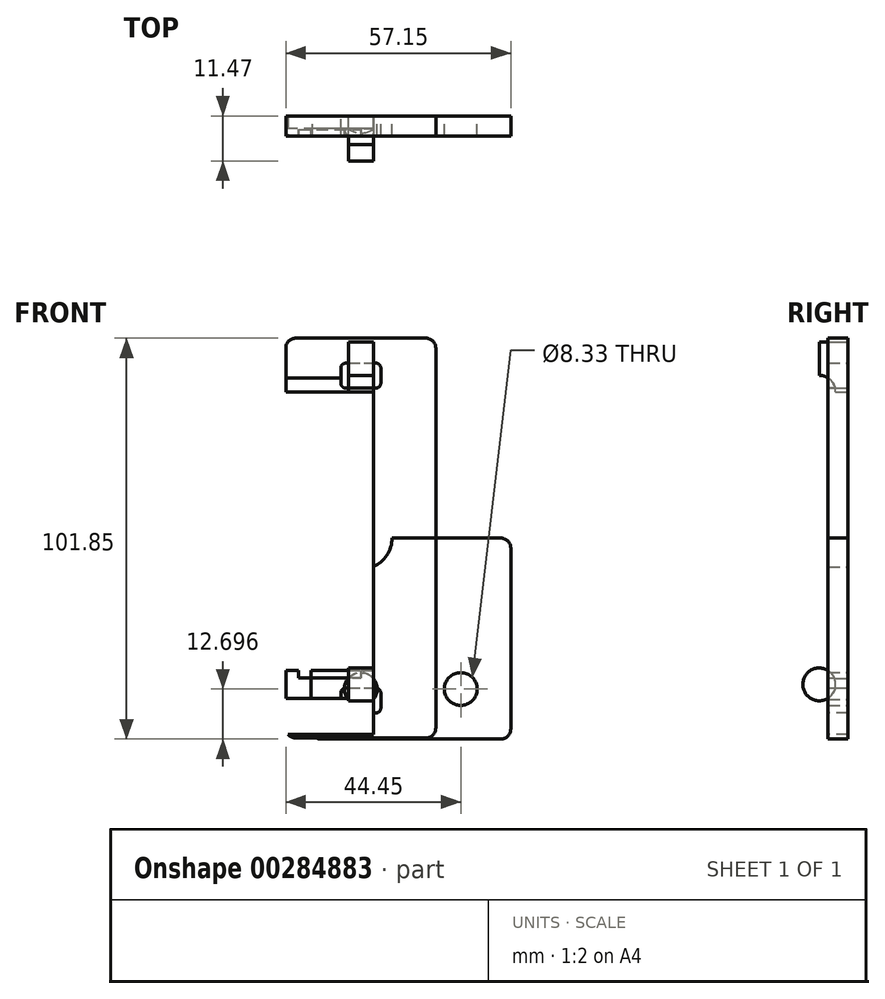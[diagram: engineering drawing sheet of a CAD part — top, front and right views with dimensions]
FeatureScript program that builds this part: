
annotation { "Feature Type Name" : "Feature", "Feature Type Description" : "" }
export const myFeature = defineFeature(function(context is Context, id is Id, definition is map)
    precondition{}
    {
        {
            var Q0;
            Q0=qCreatedBy(makeId("Front.planeOp"),FACE);
            var sketch = newSketch(context, id + "F0", { "sketchPlane" : qUnion([Q0])});
            skCircle(sketch, "E0", {"center": v(0, 0) * mm, "radius": 7.94 * mm});
            skLineSegment(sketch, "E1", {"start": v(0, 0) * mm, "end": v(0, 12.7) * mm});
            skLineSegment(sketch, "E2", {"start": v(0, 12.7) * mm, "end": v(0, 0) * mm});
            skLineSegment(sketch, "E3", {"start": v(-12.7, 0) * mm, "end": v(0, 0) * mm});
            skLineSegment(sketch, "E4", {"start": v(0, 0) * mm, "end": v(38.1, 0) * mm});
            skLineSegment(sketch, "E5", {"start": v(0, -38.35) * mm, "end": v(0, -51.05) * mm});
            skLineSegment(sketch, "E6.bottom", {"start": v(-12.7, 12.7) * mm, "end": v(38.1, 12.7) * mm});
            skLineSegment(sketch, "E6.top", {"start": v(-12.7, -51.05) * mm, "end": v(38.1, -51.05) * mm});
            skLineSegment(sketch, "E6.left", {"start": v(-12.7, 12.7) * mm, "end": v(-12.7, -51.05) * mm});
            skLineSegment(sketch, "E6.right", {"start": v(38.1, 12.7) * mm, "end": v(38.1, -51.05) * mm});
            skCircle(sketch, "E7", {"center": v(0, -38.35) * mm, "radius": 4.17 * mm});
            skCircle(sketch, "E8", {"center": v(25.4, -38.35) * mm, "radius": 4.17 * mm});
            skLineSegment(sketch, "E9", {"start": v(-4.17, -38.4) * mm, "end": v(-12.7, -38.4) * mm});
            skLineSegment(sketch, "E10", {"start": v(38.1, -38.35) * mm, "end": v(29.57, -38.35) * mm});
            skLineSegment(sketch, "E11", {"start": v(25.4, -38.35) * mm, "end": v(0, -38.35) * mm});
            skLineSegment(sketch, "E12", {"start": v(19.05, 0) * mm, "end": v(19.05, -38.35) * mm});
            skLineSegment(sketch, "E13", {"start": v(0, -38.35) * mm, "end": v(0, -10.67) * mm});
            skLineSegment(sketch, "E14", {"start": v(0, -10.67) * mm, "end": v(0, 0) * mm});
            skSolve(sketch);
        }
        {
            var Q0;
            {var subQ0=sQuery(id+"F0.wireOp",EDGE,"E9");Q0=makeQuery(id+"F0.imprint","IMPRINT",FACE,{"disambiguationData":[TD([[makeQuery(id+"F0.imprint","IMPRINT",EDGE,{"derivedFrom":subQ0}),1.0]])]});}
            var Q1;
            {var subQ3=sQuery(id+"F0.wireOp",EDGE,"E9");Q1=makeQuery(id+"F0.imprint","IMPRINT",FACE,{"disambiguationData":[TD([[makeQuery(id+"F0.imprint","IMPRINT",EDGE,{"derivedFrom":subQ3}),-1.0]])]});}
            var Q2;
            {var subQ1=sQuery(id+"F0.wireOp",EDGE,"E2");var subQ5=sQuery(id+"F0.wireOp",EDGE,"E0");var subQ6=makeQuery(id+"F0.imprint","INTERSECT",VERTEX,{"derivedFrom":[subQ5,subQ1]});Q2=makeQuery(id+"F0.imprint","IMPRINT",FACE,{"disambiguationData":[TD([[makeQuery(id+"F0.imprint","IMPRINT",EDGE,{"disambiguationData":[TD([[subQ6,-1.0]])],"derivedFrom":subQ5}),-1.0]])]});}
            var Q3;
            {var subQ1=sQuery(id+"F0.wireOp",EDGE,"E2");var subQ7=sQuery(id+"F0.wireOp",EDGE,"E0");var subQ9=makeQuery(id+"F0.imprint","INTERSECT",VERTEX,{"derivedFrom":[subQ7,subQ1]});Q3=makeQuery(id+"F0.imprint","IMPRINT",FACE,{"disambiguationData":[TD([[makeQuery(id+"F0.imprint","IMPRINT",EDGE,{"disambiguationData":[TD([[subQ9,1.0]])],"derivedFrom":subQ7}),-1.0]])]});}
            var Q4;
            Q4=makeQuery(id+"F0.imprint","IMPRINT",FACE,{"disambiguationData":[TD([[makeQuery(id+"F0.imprint","IMPRINT",EDGE,{"derivedFrom":sQuery(id+"F0.wireOp",EDGE,"E8")}),-1.0]])]});
            var Q5;
            {var subQ0=sQuery(id+"F0.wireOp",EDGE,"E12");Q5=makeQuery(id+"F0.imprint","IMPRINT",FACE,{"disambiguationData":[TD([[makeQuery(id+"F0.imprint","IMPRINT",EDGE,{"derivedFrom":subQ0}),-1.0]])]});}
            var Q6;
            {var subQ9=sQuery(id+"F0.wireOp",EDGE,"E10");Q6=makeQuery(id+"F0.imprint","IMPRINT",FACE,{"disambiguationData":[TD([[makeQuery(id+"F0.imprint","IMPRINT",EDGE,{"derivedFrom":subQ9}),1.0]])]});}
            extrude(context, id + "F1", {"entities" : qUnion([Q0, Q1, Q2, Q3, Q4, Q5, Q6]), "depth" : 5.08 * mm, "offsetDistance" : 25.4 * mm});
        }
        {
            var Q0;
            Q0=makeQuery(id+"F1.opExtrude","SWEPT_EDGE",EDGE,{"disambiguationData":[OSD([sQuery(id+"F0.wireOp",EDGE,"E6.bottom"),sQuery(id+"F0.wireOp",EDGE,"E6.right")])]});
            var Q1;
            Q1=makeQuery(id+"F1.opExtrude","SWEPT_EDGE",EDGE,{"disambiguationData":[OSD([sQuery(id+"F0.wireOp",EDGE,"E6.top"),sQuery(id+"F0.wireOp",EDGE,"E6.right")])]});
            var Q2;
            Q2=makeQuery(id+"F1.opExtrude","SWEPT_EDGE",EDGE,{"disambiguationData":[OSD([sQuery(id+"F0.wireOp",EDGE,"E6.bottom"),sQuery(id+"F0.wireOp",EDGE,"E6.left")])]});
            var Q3;
            Q3=makeQuery(id+"F1.opExtrude","SWEPT_EDGE",EDGE,{"disambiguationData":[OSD([sQuery(id+"F0.wireOp",EDGE,"E6.top"),sQuery(id+"F0.wireOp",EDGE,"E6.left")])]});
            fillet(context, id + "F2", {"entities" : qUnion([Q0, Q1, Q2, Q3]), "tangentPropagation" : true, "radius" : 2.54 * mm, "defaultsChanged" : true, "vertexSettings" : [], "allowEdgeOverflow" : false});
        }
        {
            var Q0;
            Q0=qCreatedBy(makeId("Front.planeOp"),FACE);
            var sketch = newSketch(context, id + "F3", { "sketchPlane" : qUnion([Q0])});
            skLineSegment(sketch, "E15.bottom", {"start": v(0, 0) * mm, "end": v(-19.05, 0) * mm});
            skLineSegment(sketch, "E15.top", {"start": v(0, 50.8) * mm, "end": v(-19.05, 50.8) * mm});
            skLineSegment(sketch, "E15.left", {"start": v(0, 0) * mm, "end": v(0, 50.8) * mm});
            skLineSegment(sketch, "E15.right", {"start": v(-19.05, 0) * mm, "end": v(-19.05, 50.8) * mm});
            skLineSegment(sketch, "E16.MirrorCS", {"start": v(0, -50.8) * mm, "end": v(-19.05, -50.8) * mm});
            skLineSegment(sketch, "E17.MirrorCS", {"start": v(0, 0) * mm, "end": v(0, -50.8) * mm});
            skLineSegment(sketch, "E18.MirrorCS", {"start": v(-19.05, 0) * mm, "end": v(-19.05, -50.8) * mm});
            skLineSegment(sketch, "E19.MirrorCS", {"start": v(0, 0) * mm, "end": v(19.05, 0) * mm});
            skLineSegment(sketch, "E20.MirrorCS", {"start": v(0, -50.8) * mm, "end": v(19.05, -50.8) * mm});
            skLineSegment(sketch, "E21.MirrorCS", {"start": v(0, 50.8) * mm, "end": v(19.05, 50.8) * mm});
            skLineSegment(sketch, "E22.MirrorCS", {"start": v(19.05, 0) * mm, "end": v(19.05, 50.8) * mm});
            skLineSegment(sketch, "E23.MirrorCS", {"start": v(19.05, 0) * mm, "end": v(19.05, -50.8) * mm});
            skLineSegment(sketch, "E24", {"start": v(0, 0) * mm, "end": v(0, 19.05) * mm});
            skCircle(sketch, "E25", {"center": v(0, 19.05) * mm, "radius": 2.38 * mm});
            skLineSegment(sketch, "E26.bottom", {"start": v(-19.05, 0) * mm, "end": v(-8.89, 0) * mm});
            skLineSegment(sketch, "E26.top", {"start": v(-19.05, 22.23) * mm, "end": v(-10.16, 22.23) * mm});
            skLineSegment(sketch, "E26.left", {"start": v(-19.05, 0) * mm, "end": v(-19.05, 22.23) * mm});
            skCircle(sketch, "E27", {"center": v(-10.16, 22.23) * mm, "radius": 3.57 * mm});
            skCircle(sketch, "E28.MirrorC", {"center": v(0, -19.05) * mm, "radius": 2.38 * mm});
            skCircle(sketch, "E29.MirrorC", {"center": v(-10.16, -22.23) * mm, "radius": 3.57 * mm});
            skLineSegment(sketch, "E30.bottom", {"start": v(0, 0) * mm, "end": v(-15.88, 0) * mm});
            skLineSegment(sketch, "E30.top", {"start": v(0, -35.56) * mm, "end": v(-15.87, -35.56) * mm});
            skLineSegment(sketch, "E30.left", {"start": v(0, 0) * mm, "end": v(0, -35.56) * mm});
            skLineSegment(sketch, "E30.right", {"start": v(-15.88, 0) * mm, "end": v(-15.87, -35.56) * mm});
            skLineSegment(sketch, "E31", {"start": v(0, 50.8) * mm, "end": v(0, 44.45) * mm});
            skLineSegment(sketch, "E32", {"start": v(0, 44.45) * mm, "end": v(0, 38.1) * mm});
            skLineSegment(sketch, "E33", {"start": v(0, 38.1) * mm, "end": v(-5.08, 38.1) * mm});
            skLineSegment(sketch, "E34.bottom", {"start": v(-5.08, 38.1) * mm, "end": v(0, 38.1) * mm});
            skLineSegment(sketch, "E34.top", {"start": v(-5.08, 44.45) * mm, "end": v(0, 44.45) * mm});
            skLineSegment(sketch, "E34.left", {"start": v(-5.08, 38.1) * mm, "end": v(-5.08, 44.45) * mm});
            skLineSegment(sketch, "E34.right", {"start": v(0, 38.1) * mm, "end": v(0, 44.45) * mm});
            skLineSegment(sketch, "E35.MirrorCS", {"start": v(5.08, 38.1) * mm, "end": v(0, 38.1) * mm});
            skLineSegment(sketch, "E36.MirrorCS", {"start": v(5.08, 44.45) * mm, "end": v(0, 44.45) * mm});
            skLineSegment(sketch, "E37.MirrorCS", {"start": v(0, 38.1) * mm, "end": v(5.08, 38.1) * mm});
            skLineSegment(sketch, "E38.MirrorCS", {"start": v(5.08, 38.1) * mm, "end": v(5.08, 44.45) * mm});
            skLineSegment(sketch, "E39.MirrorCS", {"start": v(0, -44.45) * mm, "end": v(0, -38.1) * mm});
            skLineSegment(sketch, "E40.MirrorCS", {"start": v(0, -38.1) * mm, "end": v(0, -44.45) * mm});
            skLineSegment(sketch, "E41.MirrorCS", {"start": v(0, -38.1) * mm, "end": v(5.08, -38.1) * mm});
            skLineSegment(sketch, "E42.MirrorCS", {"start": v(-5.08, -38.1) * mm, "end": v(0, -38.1) * mm});
            skLineSegment(sketch, "E43.MirrorCS", {"start": v(-5.08, -44.45) * mm, "end": v(0, -44.45) * mm});
            skLineSegment(sketch, "E44.MirrorCS", {"start": v(5.08, -44.45) * mm, "end": v(0, -44.45) * mm});
            skLineSegment(sketch, "E45.MirrorCS", {"start": v(5.08, -38.1) * mm, "end": v(5.08, -44.45) * mm});
            skLineSegment(sketch, "E46.MirrorCS", {"start": v(0, -38.1) * mm, "end": v(-5.08, -38.1) * mm});
            skLineSegment(sketch, "E47.MirrorCS", {"start": v(-5.08, -38.1) * mm, "end": v(-5.08, -44.45) * mm});
            skLineSegment(sketch, "E48.MirrorCS", {"start": v(5.08, -38.1) * mm, "end": v(0, -38.1) * mm});
            skSolve(sketch);
        }
        {
            var Q0;
            {var subQ12=sQuery(id+"F3.wireOp",EDGE,"E15.top");Q0=makeQuery(id+"F3.imprint","IMPRINT",FACE,{"disambiguationData":[TD([[makeQuery(id+"F3.imprint","IMPRINT",EDGE,{"derivedFrom":subQ12}),1.0]])]});}
            var Q1;
            {var subQ8=sQuery(id+"F3.wireOp",EDGE,"E26.bottom");Q1=makeQuery(id+"F3.imprint","IMPRINT",FACE,{"disambiguationData":[TD([[makeQuery(id+"F3.imprint","IMPRINT",EDGE,{"derivedFrom":subQ8}),1.0]])]});}
            var Q2;
            {var subQ1=sQuery(id+"F3.wireOp",EDGE,"E21.MirrorCS");Q2=makeQuery(id+"F3.imprint","IMPRINT",FACE,{"disambiguationData":[TD([[makeQuery(id+"F3.imprint","IMPRINT",EDGE,{"derivedFrom":subQ1}),-1.0]])]});}
            var Q3;
            Q3=makeQuery(id+"F3.imprint","IMPRINT",FACE,{"disambiguationData":[TD([[makeQuery(id+"F3.imprint","IMPRINT",EDGE,{"derivedFrom":sQuery(id+"F3.wireOp",EDGE,"E20.MirrorCS")}),1.0]])]});
            var Q4;
            Q4=makeQuery(id+"F3.imprint","IMPRINT",FACE,{"disambiguationData":[TD([[makeQuery(id+"F3.imprint","IMPRINT",EDGE,{"derivedFrom":sQuery(id+"F3.wireOp",EDGE,"E16.MirrorCS")}),-1.0]])]});
            var Q5;
            Q5=makeQuery(id+"F3.imprint","IMPRINT",FACE,{"disambiguationData":[TD([[makeQuery(id+"F3.imprint","IMPRINT",EDGE,{"derivedFrom":sQuery(id+"F3.wireOp",EDGE,"E29.MirrorC")}),1.0]])]});
            extrude(context, id + "F4", {"entities" : qUnion([Q0, Q1, Q2, Q3, Q4, Q5]), "depth" : 5.08 * mm, "offsetDistance" : 25.4 * mm});
        }
        {
            var Q0;
            Q0=makeQuery(id+"F4.opExtrude","SWEPT_EDGE",EDGE,{"disambiguationData":[OSD([sQuery(id+"F3.wireOp",EDGE,"E21.MirrorCS"),sQuery(id+"F3.wireOp",EDGE,"E22.MirrorCS")])]});
            var Q1;
            Q1=makeQuery(id+"F4.opExtrude","SWEPT_EDGE",EDGE,{"disambiguationData":[OSD([sQuery(id+"F3.wireOp",EDGE,"E15.top"),sQuery(id+"F3.wireOp",EDGE,"E15.right")])]});
            var Q2;
            Q2=makeQuery(id+"F4.opExtrude","SWEPT_EDGE",EDGE,{"disambiguationData":[OSD([sQuery(id+"F3.wireOp",EDGE,"E16.MirrorCS"),sQuery(id+"F3.wireOp",EDGE,"E18.MirrorCS")])]});
            var Q3;
            Q3=makeQuery(id+"F4.opExtrude","SWEPT_EDGE",EDGE,{"disambiguationData":[OSD([sQuery(id+"F3.wireOp",EDGE,"E20.MirrorCS"),sQuery(id+"F3.wireOp",EDGE,"E23.MirrorCS")])]});
            fillet(context, id + "F5", {"entities" : qUnion([Q0, Q1, Q2, Q3]), "tangentPropagation" : true, "radius" : 2.54 * mm, "defaultsChanged" : false, "vertexSettings" : [], "allowEdgeOverflow" : false});
        }
        {
            var Q0;
            Q0=makeQuery(id+"F4.opExtrude","SWEPT_EDGE",EDGE,{"disambiguationData":[OSD([sQuery(id+"F3.wireOp",EDGE,"E36.MirrorCS"),sQuery(id+"F3.wireOp",EDGE,"E38.MirrorCS")])]});
            var Q1;
            Q1=makeQuery(id+"F4.opExtrude","SWEPT_EDGE",EDGE,{"disambiguationData":[OSD([sQuery(id+"F3.wireOp",EDGE,"E37.MirrorCS"),sQuery(id+"F3.wireOp",EDGE,"E38.MirrorCS")])]});
            var Q2;
            Q2=makeQuery(id+"F4.opExtrude","SWEPT_EDGE",EDGE,{"disambiguationData":[OSD([sQuery(id+"F3.wireOp",EDGE,"E34.top"),sQuery(id+"F3.wireOp",EDGE,"E34.left")])]});
            var Q3;
            Q3=makeQuery(id+"F4.opExtrude","SWEPT_EDGE",EDGE,{"disambiguationData":[OSD([sQuery(id+"F3.wireOp",EDGE,"E34.bottom"),sQuery(id+"F3.wireOp",EDGE,"E34.left")])]});
            var Q4;
            Q4=makeQuery(id+"F4.opExtrude","SWEPT_EDGE",EDGE,{"disambiguationData":[OSD([sQuery(id+"F3.wireOp",EDGE,"E45.MirrorCS"),sQuery(id+"F3.wireOp",EDGE,"E48.MirrorCS")])]});
            var Q5;
            Q5=makeQuery(id+"F4.opExtrude","SWEPT_EDGE",EDGE,{"disambiguationData":[OSD([sQuery(id+"F3.wireOp",EDGE,"E46.MirrorCS"),sQuery(id+"F3.wireOp",EDGE,"E47.MirrorCS")])]});
            var Q6;
            Q6=makeQuery(id+"F4.opExtrude","SWEPT_EDGE",EDGE,{"disambiguationData":[OSD([sQuery(id+"F3.wireOp",EDGE,"E44.MirrorCS"),sQuery(id+"F3.wireOp",EDGE,"E45.MirrorCS")])]});
            var Q7;
            Q7=makeQuery(id+"F4.opExtrude","SWEPT_EDGE",EDGE,{"disambiguationData":[OSD([sQuery(id+"F3.wireOp",EDGE,"E43.MirrorCS"),sQuery(id+"F3.wireOp",EDGE,"E47.MirrorCS")])]});
            fillet(context, id + "F6", {"entities" : qUnion([Q0, Q1, Q2, Q3, Q4, Q5, Q6, Q7]), "tangentPropagation" : true, "radius" : 1.27 * mm, "defaultsChanged" : false, "vertexSettings" : [], "allowEdgeOverflow" : false});
        }
        {
            var Q0;
            Q0=qCreatedBy(makeId("Front.planeOp"),FACE);
            var sketch = newSketch(context, id + "F7", { "sketchPlane" : qUnion([Q0])});
            skLineSegment(sketch, "E49.bottom", {"start": v(0, 0) * mm, "end": v(3.18, 0) * mm});
            skLineSegment(sketch, "E49.top", {"start": v(0, 49.87) * mm, "end": v(3.17, 49.87) * mm});
            skLineSegment(sketch, "E49.left", {"start": v(0, 0) * mm, "end": v(0, 49.87) * mm});
            skLineSegment(sketch, "E49.right", {"start": v(3.18, 0) * mm, "end": v(3.17, 49.87) * mm});
            skLineSegment(sketch, "E50.MirrorCS", {"start": v(0, 0) * mm, "end": v(-3.18, 0) * mm});
            skLineSegment(sketch, "E51.MirrorCS", {"start": v(0, 49.87) * mm, "end": v(-3.17, 49.87) * mm});
            skLineSegment(sketch, "E52.MirrorCS", {"start": v(-3.18, 0) * mm, "end": v(-3.17, 49.87) * mm});
            skLineSegment(sketch, "E53.MirrorCS", {"start": v(0, -49.87) * mm, "end": v(-3.17, -49.87) * mm});
            skLineSegment(sketch, "E54.MirrorCS", {"start": v(0, -49.87) * mm, "end": v(3.17, -49.87) * mm});
            skLineSegment(sketch, "E55.MirrorCS", {"start": v(0, 0) * mm, "end": v(0, -49.87) * mm});
            skLineSegment(sketch, "E56.MirrorCS", {"start": v(-3.18, 0) * mm, "end": v(-3.17, -49.87) * mm});
            skLineSegment(sketch, "E57.MirrorCS", {"start": v(3.18, 0) * mm, "end": v(3.17, -49.87) * mm});
            skLineSegment(sketch, "E58", {"start": v(0, 49.87) * mm, "end": v(0, 24.47) * mm});
            skCircle(sketch, "E59", {"center": v(0, 24.47) * mm, "radius": 1.59 * mm});
            skCircle(sketch, "E60.MirrorC", {"center": v(0, -24.47) * mm, "radius": 1.59 * mm});
            skSolve(sketch);
        }
        {
            var Q0;
            Q0 = qSketchRegion(id + "F7", true);
            extrude(context, id + "F8", {"entities" : qUnion([Q0]), "depth" : 19.1 * mm, "offsetDistance" : 25.4 * mm});
        }
        {
            var Q0;
            Q0=makeQuery(id+"F8.opExtrude","SWEPT_FACE",FACE,{"disambiguationData":[OSD([sQuery(id+"F7.wireOp",EDGE,"E49.right"),sQuery(id+"F7.wireOp",EDGE,"E57.MirrorCS")])]});
            var sketch = newSketch(context, id + "F9", { "sketchPlane" : qUnion([Q0])});
            skLineSegment(sketch, "E61.bottom", {"start": v(0, 49.87) * mm, "end": v(-7.3, 49.87) * mm});
            skLineSegment(sketch, "E61.top", {"start": v(0, 37.17) * mm, "end": v(-7.3, 37.17) * mm});
            skLineSegment(sketch, "E61.left", {"start": v(0, 49.87) * mm, "end": v(0, 37.17) * mm});
            skLineSegment(sketch, "E61.right", {"start": v(-7.3, 49.87) * mm, "end": v(-7.3, 37.17) * mm});
            skCircle(sketch, "E62", {"center": v(-7.3, 37.17) * mm, "radius": 4.17 * mm});
            skLineSegment(sketch, "E63", {"start": v(0, 0) * mm, "end": v(-6.41, 0) * mm});
            skCircle(sketch, "E64.MirrorC", {"center": v(-7.3, -37.17) * mm, "radius": 4.17 * mm});
            skSolve(sketch);
        }
        {
            var Q0;
            Q0=makeQuery(id+"F9.imprint","IMPRINT",FACE,{"disambiguationData":[TD([[makeQuery(id+"F9.imprint","IMPRINT",EDGE,{"derivedFrom":sQuery(id+"F9.wireOp",EDGE,"QnUiYRWN-gcmX-vHxJ-j9Zo-fiwyTM2SN61R")}),1.0]])]});
            var Q1;
            Q1=makeQuery(id+"F9.imprint","IMPRINT",FACE,{"disambiguationData":[TD([[makeQuery(id+"F9.imprint","IMPRINT",EDGE,{"derivedFrom":sQuery(id+"F9.wireOp",EDGE,"E64.MirrorC")}),-1.0]])]});
            var Q2;
            {var subQ0=sQuery(id+"F9.wireOp",EDGE,"E61.right");var subQ1=sQuery(id+"F9.wireOp",EDGE,"E61.top");var subQ2=makeQuery(id+"F9.imprint","INTERSECT",VERTEX,{"derivedFrom":[subQ1,subQ0]});Q2=makeQuery(id+"F9.imprint","IMPRINT",FACE,{"disambiguationData":[TD([[makeQuery(id+"F9.imprint","IMPRINT",EDGE,{"disambiguationData":[TD([[subQ2,1.0]])],"derivedFrom":subQ1}),-1.0]])]});}
            var Q3;
            {var subQ0=sQuery(id+"F9.wireOp",EDGE,"E61.right");var subQ1=sQuery(id+"F9.wireOp",EDGE,"E61.top");var subQ2=makeQuery(id+"F9.imprint","INTERSECT",VERTEX,{"derivedFrom":[subQ1,subQ0]});Q3=makeQuery(id+"F9.imprint","IMPRINT",FACE,{"disambiguationData":[TD([[makeQuery(id+"F9.imprint","IMPRINT",EDGE,{"disambiguationData":[TD([[subQ2,1.0]])],"derivedFrom":subQ1}),1.0]])]});}
            extrude(context, id + "F10", {"entities" : qUnion([Q0, Q1, Q2, Q3]), "operationType" : NewBodyOperationType.REMOVE, "oppositeDirection" : true, "depth" : 25.4 * mm, "offsetDistance" : 25.4 * mm});
        }
    });
